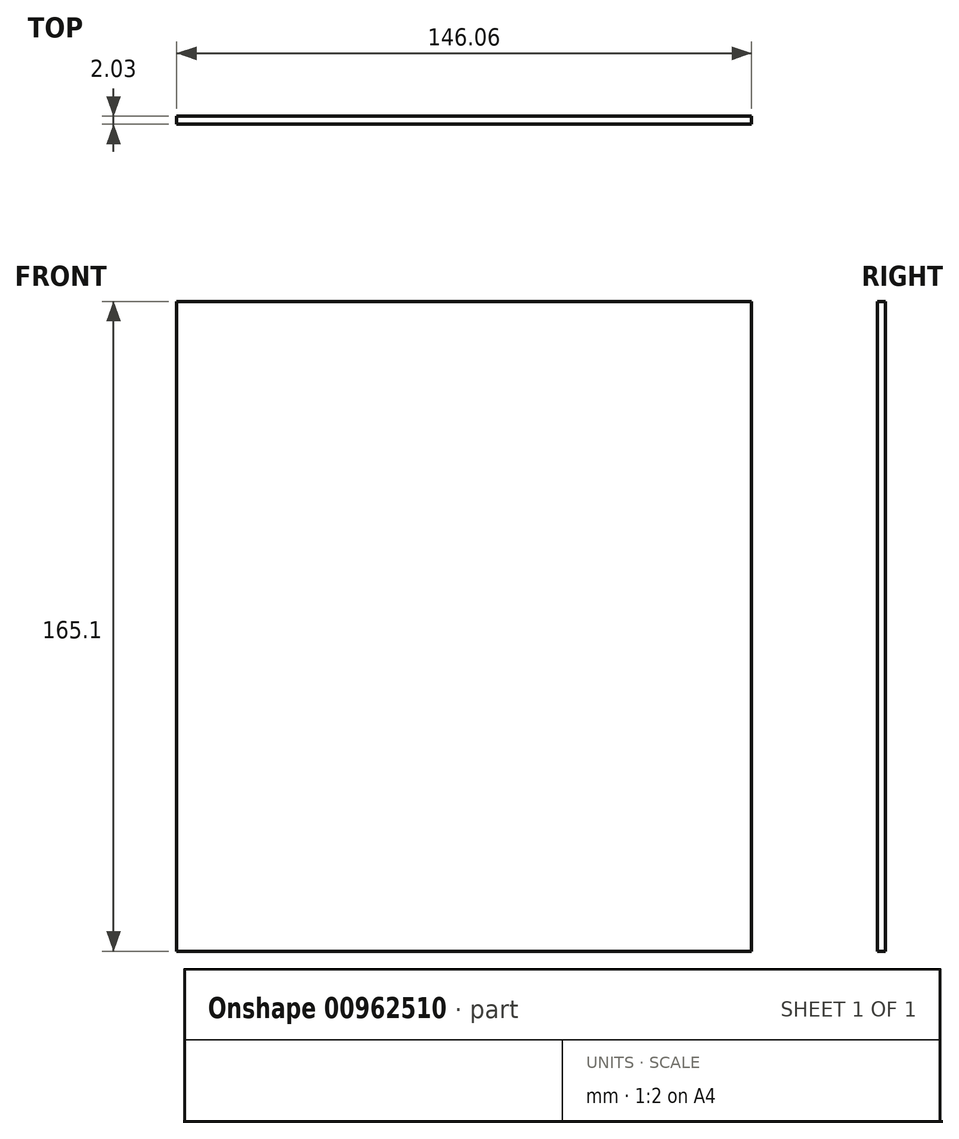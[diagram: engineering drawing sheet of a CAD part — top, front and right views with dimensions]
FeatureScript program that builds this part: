
annotation { "Feature Type Name" : "Feature", "Feature Type Description" : "" }
export const myFeature = defineFeature(function(context is Context, id is Id, definition is map)
    precondition{}
    {
        {
            var Q0;
            Q0=qCreatedBy(makeId("Front.planeOp"),FACE);
            var sketch = newSketch(context, id + "F0", { "sketchPlane" : qUnion([Q0])});
            skLineSegment(sketch, "E0.bottom", {"start": v(73.03, 82.55) * mm, "end": v(-73.03, 82.55) * mm});
            skLineSegment(sketch, "E0.top", {"start": v(73.03, -82.55) * mm, "end": v(-73.03, -82.55) * mm});
            skLineSegment(sketch, "E0.left", {"start": v(73.03, 82.55) * mm, "end": v(73.03, -82.55) * mm});
            skLineSegment(sketch, "E0.right", {"start": v(-73.03, 82.55) * mm, "end": v(-73.03, -82.55) * mm});
            skPoint(sketch, "E0.middle", {"position": v(0, 0) * mm});
            skSolve(sketch);
        }
        {
            var Q0;
            Q0=makeQuery(id+"F0.imprint","IMPRINT",FACE,{"disambiguationData":[TD([[makeQuery(id+"F0.imprint","IMPRINT",EDGE,{"derivedFrom":sQuery(id+"F0.wireOp",EDGE,"E0.bottom")}),1.0]])]});
            extrude(context, id + "F1", {"entities" : qUnion([Q0]), "depth" : 2.03 * mm, "offsetDistance" : 25.4 * mm});
        }
    });
